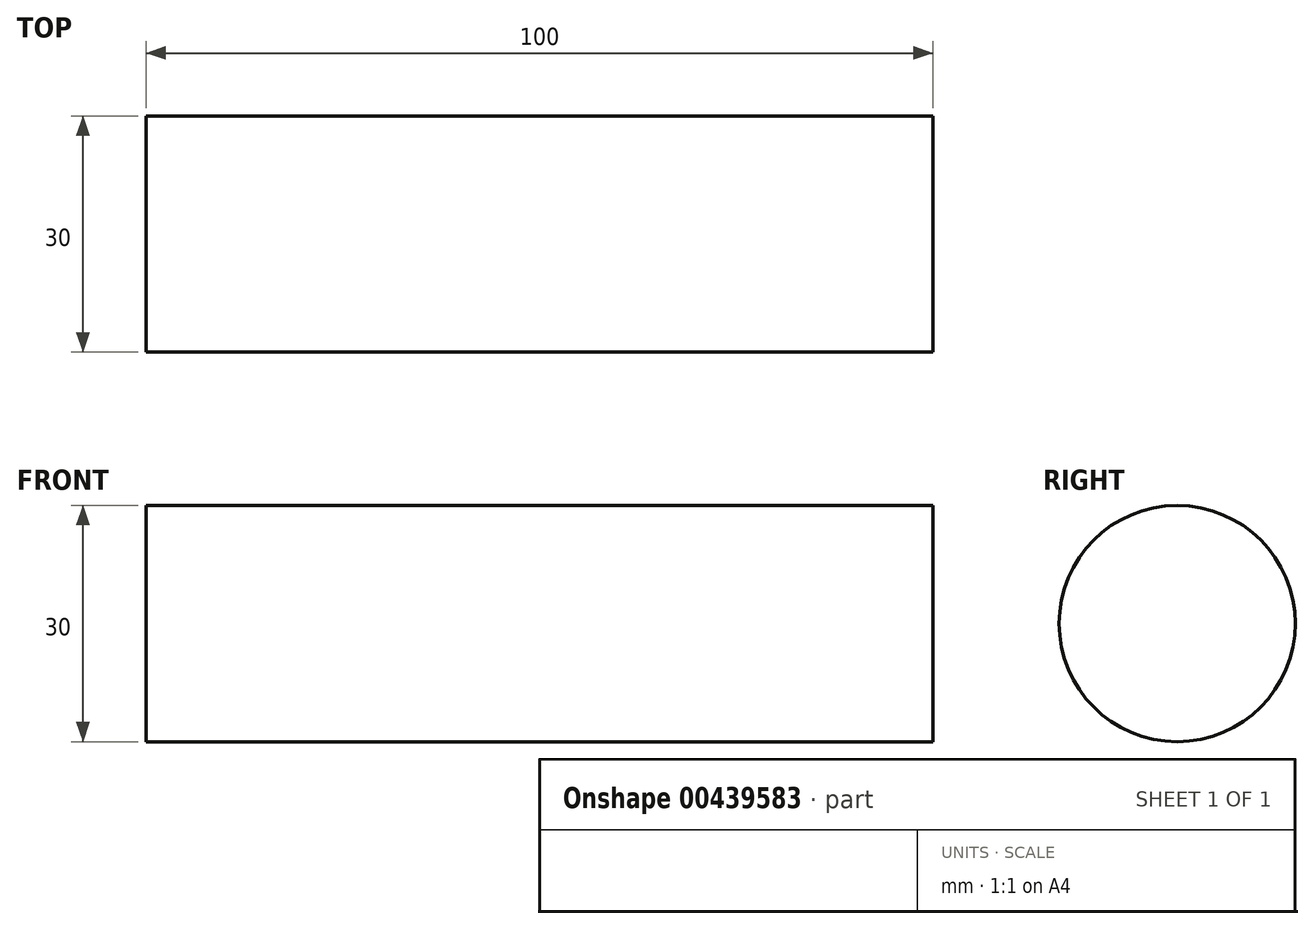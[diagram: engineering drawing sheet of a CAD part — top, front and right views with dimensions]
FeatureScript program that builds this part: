
annotation { "Feature Type Name" : "Feature", "Feature Type Description" : "" }
export const myFeature = defineFeature(function(context is Context, id is Id, definition is map)
    precondition{}
    {
        {
            var Q0;
            Q0=qCreatedBy(makeId("Top.planeOp"),FACE);
            var sketch = newSketch(context, id + "F0", { "sketchPlane" : qUnion([Q0])});
            skLineSegment(sketch, "E0", {"start": v(-69.31, 0) * mm, "end": v(61.46, 0) * mm, "construction": true});
            skLineSegment(sketch, "E1.bottom", {"start": v(-70, 0) * mm, "end": v(30, 0) * mm});
            skLineSegment(sketch, "E1.top", {"start": v(-70, 15) * mm, "end": v(30, 15) * mm});
            skLineSegment(sketch, "E1.left", {"start": v(-70, 0) * mm, "end": v(-70, 15) * mm});
            skLineSegment(sketch, "E1.right", {"start": v(30, 0) * mm, "end": v(30, 15) * mm});
            skSolve(sketch);
        }
        {
            var Q0;
            Q0 = qSketchRegion(id + "F0", true);
            var Q1;
            Q1=sQuery(id+"F0.wireOp",EDGE,"E0");
            revolve(context, id + "F1", {"entities" : qUnion([Q0]), "axis" : qUnion([Q1]), "revolveType" : RevolveType.FULL});
        }
    });
